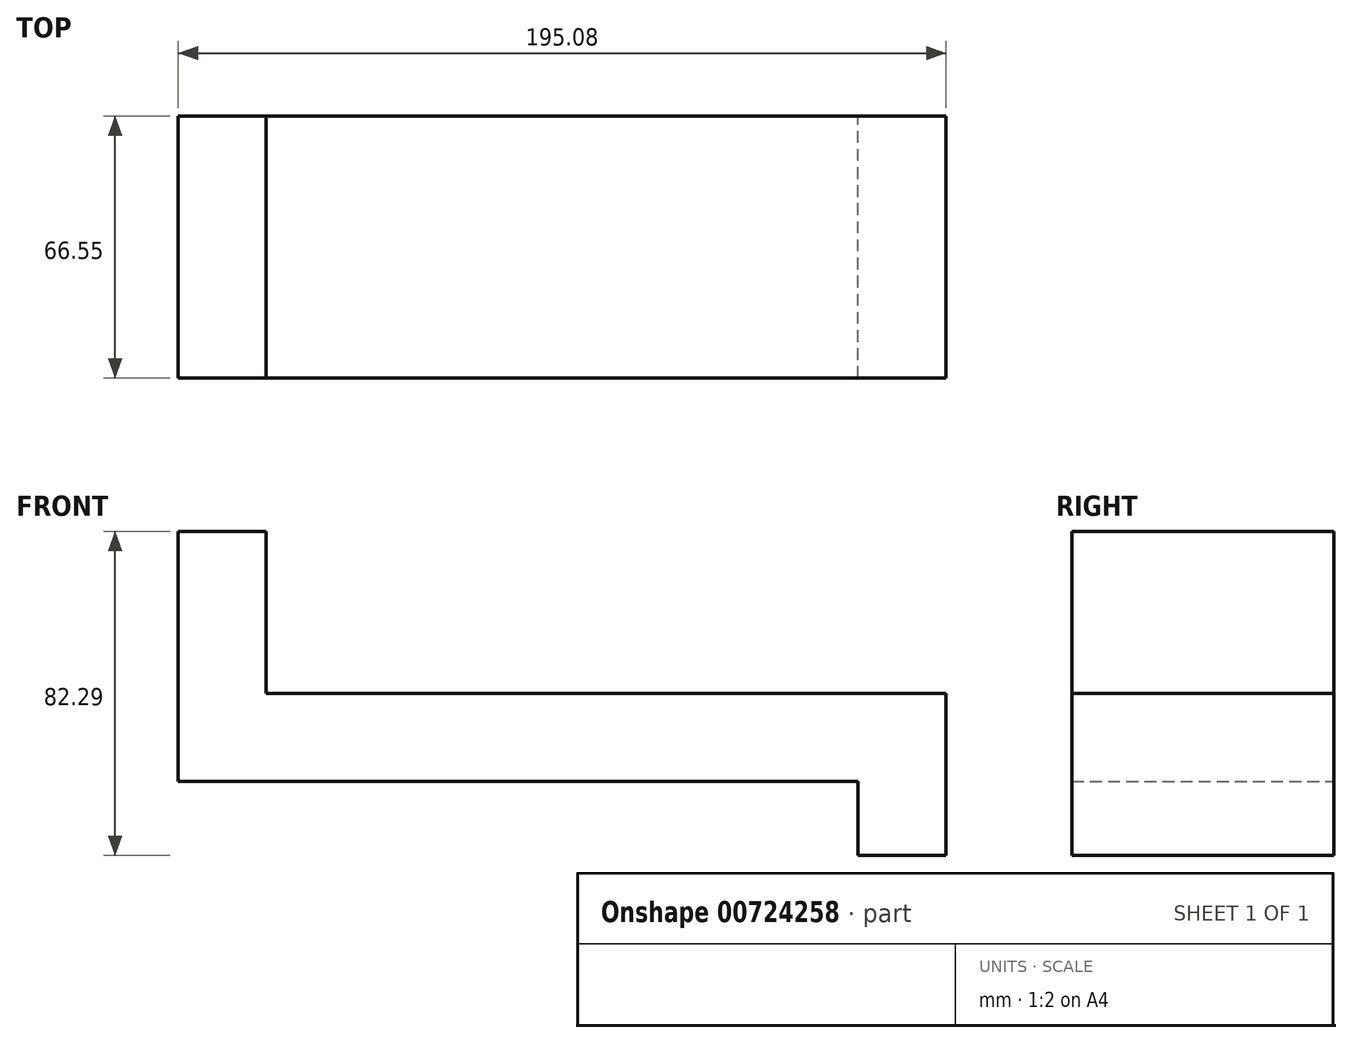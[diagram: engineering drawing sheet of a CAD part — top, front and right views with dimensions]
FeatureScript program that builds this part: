
annotation { "Feature Type Name" : "Feature", "Feature Type Description" : "" }
export const myFeature = defineFeature(function(context is Context, id is Id, definition is map)
    precondition{}
    {
        {
            var Q0;
            Q0=qCreatedBy(makeId("Front.planeOp"),FACE);
            var sketch = newSketch(context, id + "F0", { "sketchPlane" : qUnion([Q0])});
            skLineSegment(sketch, "E0", {"start": v(-60.48, 85.61) * mm, "end": v(-82.84, 85.61) * mm});
            skLineSegment(sketch, "E1", {"start": v(-82.84, 85.61) * mm, "end": v(-82.84, 22.11) * mm});
            skLineSegment(sketch, "E2", {"start": v(-60.48, 85.61) * mm, "end": v(-60.48, 44.47) * mm});
            skLineSegment(sketch, "E3", {"start": v(-82.84, 22.11) * mm, "end": v(67.53, 22.11) * mm});
            skLineSegment(sketch, "E4", {"start": v(-60.48, 44.47) * mm, "end": v(112.24, 44.47) * mm});
            skLineSegment(sketch, "E5", {"start": v(112.24, 44.47) * mm, "end": v(112.24, 3.32) * mm});
            skLineSegment(sketch, "E6", {"start": v(112.24, 3.32) * mm, "end": v(89.88, 3.32) * mm});
            skLineSegment(sketch, "E7", {"start": v(89.88, 3.32) * mm, "end": v(89.88, 22.11) * mm});
            skLineSegment(sketch, "E8", {"start": v(67.53, 22.11) * mm, "end": v(89.88, 22.11) * mm});
            skSolve(sketch);
        }
        {
            var Q0;
            Q0=makeQuery(id+"F0.imprint","IMPRINT",FACE,{"disambiguationData":[TD([[makeQuery(id+"F0.imprint","IMPRINT",EDGE,{"derivedFrom":sQuery(id+"F0.wireOp",EDGE,"E0")}),1.0]])]});
            extrude(context, id + "F1", {"entities" : qUnion([Q0]), "depth" : 66.55 * mm, "offsetDistance" : 25.4 * mm});
        }
    });
